# Revit family: PLANK_BON_TABLE
name_source: partatom
category: Arredi
units: mm (PartAtom-declared; Revit-internal decimal feet)

## family parameters
Condiviso = No
Host = Superficie
Punto di calcolo locali = No
Taglio con vuoti quando caricato = No

## types (36) — shared parameters
AVAILABLE FINISHES = Base in the colors black, white or grey aluminum. Table top in high pressure laminate (HPL) Full Colour or in MDF powder coated in black or white. Gliders in plastic.
BADGE = https://bim.archiproducts.com
COLLECTION = Bon
MATERIAL DESCRIPTION = Cast iron base and metal column powder coated
Modello = BON
PRODUCT SHEET = https://www.archiproducts.com
Produttore = PLANK
Prospetto di default = 1219 mm
TECHNICAL SHEET = https://www.plank.it
URL = https://www.plank.it

## per-type parameters (varying)
| type | BODY MATERIAL | DIAMETER | Descrizione | HEIGHT | PRODUCT CODE | STRUCTURE MATERIAL | radius |
| ⌀ 60cm, h 50cm - HPL 10mm BLACK, BLACK BASE | PLANK_HPL_BLACK | 600 mm | Round coffee table with cast iron base and HPL top | 500 mm | 9380-51 | PLANK_STEEL_POWDER_COATED_BLACK | 300 mm |
| ⌀ 60cm, h 50cm - HPL 10mm BLACK, WHITE BASE | PLANK_HPL_BLACK | 600 mm | Round coffee table with cast iron base and HPL top | 500 mm | 9380-51 | PLANK_STEEL_POWDER_COATED_WHITE | 300 mm |
| ⌀ 60cm, h 50cm - HPL 10mm BLACK, GREY BASE | PLANK_HPL_BLACK | 600 mm | Round coffee table with cast iron base and HPL top | 500 mm | 9380-51 | PLANK_STEEL_POWDER_COATED_GREY | 300 mm |
| ⌀ 60cm, h 50cm - HPL 10mm WHITE, BLACK BASE | PLANK_HPL_WHITE | 600 mm | Round coffee table with cast iron base and HPL top | 500 mm | 9380-51 | PLANK_STEEL_POWDER_COATED_BLACK | 300 mm |
| ⌀ 60cm, h 50cm - HPL 10mm WHITE, WHITE BASE | PLANK_HPL_WHITE | 600 mm | Round coffee table with cast iron base and HPL top | 500 mm | 9380-51 | PLANK_STEEL_POWDER_COATED_WHITE | 300 mm |
| ⌀ 60cm, h 50cm - HPL 10mm WHITE, GREY BASE | PLANK_HPL_WHITE | 600 mm | Round coffee table with cast iron base and HPL top | 500 mm | 9380-51 | PLANK_STEEL_POWDER_COATED_GREY | 300 mm |
| ⌀ 60cm, h 73cm - HPL 10mm BLACK, BLACK BASE | PLANK_HPL_BLACK | 600 mm | Round high side table with cast iron base and HPL top | 730 mm | 9380-01 | PLANK_STEEL_POWDER_COATED_BLACK | 300 mm |
| ⌀ 60cm, h 73cm - HPL 10mm BLACK, WHITE BASE | PLANK_HPL_BLACK | 600 mm | Round high side table with cast iron base and HPL top | 730 mm | 9380-01 | PLANK_STEEL_POWDER_COATED_WHITE | 300 mm |
| ⌀ 60cm, h 73cm - HPL 10mm BLACK, GREY BASE | PLANK_HPL_BLACK | 600 mm | Round high side table with cast iron base and HPL top | 730 mm | 9380-01 | PLANK_STEEL_POWDER_COATED_GREY | 300 mm |
| ⌀ 60cm, h 73cm - HPL 10mm WHITE, BLACK BASE | PLANK_HPL_WHITE | 600 mm | Round high side table with cast iron base and HPL top | 730 mm | 9380-01 | PLANK_STEEL_POWDER_COATED_BLACK | 300 mm |
| ⌀ 60cm, h 73cm - HPL 10mm WHITE, WHITE BASE | PLANK_HPL_WHITE | 600 mm | Round high side table with cast iron base and HPL top | 730 mm | 9380-01 | PLANK_STEEL_POWDER_COATED_WHITE | 300 mm |
| ⌀ 60cm, h 73cm - HPL 10mm WHITE, GREY BASE | PLANK_HPL_WHITE | 600 mm | Round high side table with cast iron base and HPL top | 730 mm | 9380-01 | PLANK_STEEL_POWDER_COATED_GREY | 300 mm |
| ⌀ 60cm, h 108cm - HPL 10mm BLACK, BLACK BASE | PLANK_HPL_BLACK | 600 mm | Round table with cast iron base and HPL top | 1080 mm | 9380-71 | PLANK_STEEL_POWDER_COATED_BLACK | 300 mm |
| ⌀ 60cm, h 108cm - HPL 10mm BLACK, WHITE BASE | PLANK_HPL_BLACK | 600 mm | Round table with cast iron base and HPL top | 1080 mm | 9380-71 | PLANK_STEEL_POWDER_COATED_WHITE | 300 mm |
| ⌀ 60cm, h 108cm - HPL 10mm BLACK, GREY BASE | PLANK_HPL_BLACK | 600 mm | Round table with cast iron base and HPL top | 1080 mm | 9380-71 | PLANK_STEEL_POWDER_COATED_GREY | 300 mm |
| ⌀ 60cm, h 108cm - HPL 10mm WHITE, BLACK BASE | PLANK_HPL_WHITE | 600 mm | Round table with cast iron base and HPL top | 1080 mm | 9380-71 | PLANK_STEEL_POWDER_COATED_BLACK | 300 mm |
| ⌀ 60cm, h 108cm - HPL 10mm WHITE, WHITE BASE | PLANK_HPL_WHITE | 600 mm | Round table with cast iron base and HPL top | 1080 mm | 9380-71 | PLANK_STEEL_POWDER_COATED_WHITE | 300 mm |
| ⌀ 60cm, h 108cm - HPL 10mm WHITE, GREY BASE | PLANK_HPL_WHITE | 600 mm | Round table with cast iron base and HPL top | 1080 mm | 9380-71 | PLANK_STEEL_POWDER_COATED_GREY | 300 mm |
| ⌀ 70cm, h 50cm - HPL 10mm BLACK, BLACK BASE | PLANK_HPL_BLACK | 700 mm | Round coffee table with cast iron base and HPL top | 500 mm | 9382-51 | PLANK_STEEL_POWDER_COATED_BLACK | 350 mm |
| ⌀ 70cm, h 50cm - HPL 10mm BLACK, WHITE BASE | PLANK_HPL_BLACK | 700 mm | Round coffee table with cast iron base and HPL top | 500 mm | 9382-51 | PLANK_STEEL_POWDER_COATED_WHITE | 350 mm |
| ⌀ 70cm, h 50cm - HPL 10mm BLACK, GREY BASE | PLANK_HPL_BLACK | 700 mm | Round coffee table with cast iron base and HPL top | 500 mm | 9382-51 | PLANK_STEEL_POWDER_COATED_GREY | 350 mm |
| ⌀ 70cm, h 50cm - HPL 10mm WHITE, BLACK BASE | PLANK_HPL_WHITE | 700 mm | Round coffee table with cast iron base and HPL top | 500 mm | 9382-51 | PLANK_STEEL_POWDER_COATED_BLACK | 350 mm |
| ⌀ 70cm, h 50cm - HPL 10mm WHITE, WHITE BASE | PLANK_HPL_WHITE | 700 mm | Round coffee table with cast iron base and HPL top | 500 mm | 9382-51 | PLANK_STEEL_POWDER_COATED_WHITE | 350 mm |
| ⌀ 70cm, h 50cm - HPL 10mm WHITE, GREY BASE | PLANK_HPL_WHITE | 700 mm | Round coffee table with cast iron base and HPL top | 500 mm | 9382-51 | PLANK_STEEL_POWDER_COATED_GREY | 350 mm |
| ⌀ 70cm, h 73cm - HPL 10mm BLACK, BLACK BASE | PLANK_HPL_BLACK | 700 mm | Round high side table with cast iron base and HPL top | 730 mm | 9382-01 | PLANK_STEEL_POWDER_COATED_BLACK | 350 mm |
| ⌀ 70cm, h 73cm - HPL 10mm BLACK, WHITE BASE | PLANK_HPL_BLACK | 700 mm | Round high side table with cast iron base and HPL top | 730 mm | 9382-01 | PLANK_STEEL_POWDER_COATED_WHITE | 350 mm |
| ⌀ 70cm, h 73cm - HPL 10mm BLACK, GREY BASE | PLANK_HPL_BLACK | 700 mm | Round high side table with cast iron base and HPL top | 730 mm | 9382-01 | PLANK_STEEL_POWDER_COATED_GREY | 350 mm |
| ⌀ 70cm, h 73cm - HPL 10mm WHITE, BLACK BASE | PLANK_HPL_WHITE | 700 mm | Round high side table with cast iron base and HPL top | 730 mm | 9382-01 | PLANK_STEEL_POWDER_COATED_BLACK | 350 mm |
| ⌀ 70cm, h 73cm - HPL 10mm WHITE, WHITE BASE | PLANK_HPL_WHITE | 700 mm | Round high side table with cast iron base and HPL top | 730 mm | 9382-01 | PLANK_STEEL_POWDER_COATED_WHITE | 350 mm |
| ⌀ 70cm, h 73cm - HPL 10mm WHITE, GREY BASE | PLANK_HPL_WHITE | 700 mm | Round high side table with cast iron base and HPL top | 730 mm | 9382-01 | PLANK_STEEL_POWDER_COATED_GREY | 350 mm |
| ⌀ 70cm, h 108cm - HPL 10mm BLACK, BLACK BASE | PLANK_HPL_BLACK | 700 mm | Round table with cast iron base and HPL top | 1080 mm | 9382-71 | PLANK_STEEL_POWDER_COATED_BLACK | 350 mm |
| ⌀ 70cm, h 108cm - HPL 10mm BLACK, WHITE BASE | PLANK_HPL_BLACK | 700 mm | Round table with cast iron base and HPL top | 1080 mm | 9382-71 | PLANK_STEEL_POWDER_COATED_WHITE | 350 mm |
| ⌀ 70cm, h 108cm - HPL 10mm BLACK, GREY BASE | PLANK_HPL_BLACK | 700 mm | Round table with cast iron base and HPL top | 1080 mm | 9382-71 | PLANK_STEEL_POWDER_COATED_GREY | 350 mm |
| ⌀ 70cm, h 108cm - HPL 10mm WHITE, BLACK BASE | PLANK_HPL_BLACK | 700 mm | Round table with cast iron base and HPL top | 1080 mm | 9382-71 | PLANK_STEEL_POWDER_COATED_BLACK | 350 mm |
| ⌀ 70cm, h 108cm - HPL 10mm WHITE, WHITE BASE | PLANK_HPL_WHITE | 700 mm | Round table with cast iron base and HPL top | 1080 mm | 9382-71 | PLANK_STEEL_POWDER_COATED_WHITE | 350 mm |
| ⌀ 70cm, h 108cm - HPL 10mm WHITE, GREY BASE | PLANK_HPL_BLACK | 700 mm | Round table with cast iron base and HPL top | 1080 mm | 9382-71 | PLANK_STEEL_POWDER_COATED_GREY | 350 mm |
